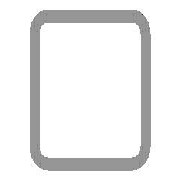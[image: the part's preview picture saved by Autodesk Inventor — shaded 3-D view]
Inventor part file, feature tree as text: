
AUTODESK INVENTOR PART (.ipt)
format: ipt  version: 2025 (Build 290162010, 162A)  size: 133,632 bytes
history: native  units: mm (DEFAULTED — no unit token found)
features: other x4, sketch x1, plane x1
ambient origin geometry x8: Origin, YZ Plane, XZ Plane, XY Plane, X Axis, Y Axis, Z Axis, Center Point
bodies: Solid1 (feature_tree), Body (feature_tree)
feature tree (6):
  parser-record x1  (decoder bookkeeping rows leaked as tree rows — omitted from the tree; the rows remain in map.json)
  other  "Driven Length"
  other  "Start Plane"
  other  "End Plane"
  sketch  "Sketch3"  dims[d3=1460.0mm d4=0.0mm d7=4.0mm d9=40.0mm d11=40.0mm d12=2.0mm d13=-0.0mm d14=1460.0mm d15=20.0mm d16=20.0mm d17=90.0deg d18=1460.0mm]
  plane  "Work Plane3"
